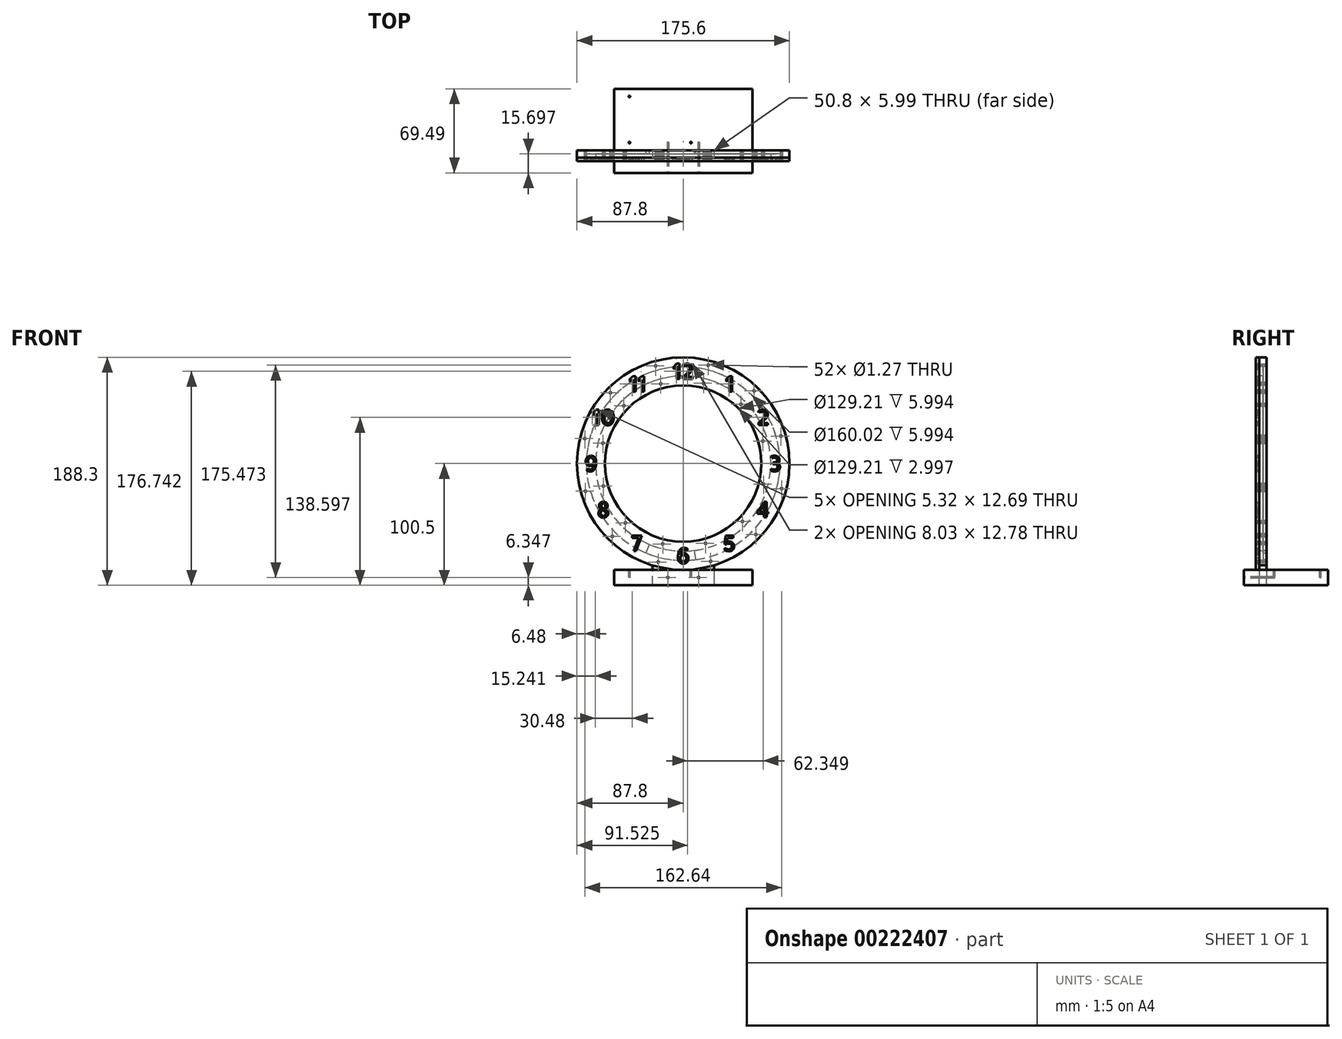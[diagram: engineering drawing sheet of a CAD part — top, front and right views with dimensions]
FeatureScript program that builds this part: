
annotation { "Feature Type Name" : "Feature", "Feature Type Description" : "" }
export const myFeature = defineFeature(function(context is Context, id is Id, definition is map)
    precondition{}
    {
        {
            var Q0;
            Q0=qCreatedBy(makeId("Front.planeOp"),FACE);
            var sketch = newSketch(context, id + "F0", { "sketchPlane" : qUnion([Q0])});
            skCircle(sketch, "E0", {"center": v(0, 0) * mm, "radius": 76.2 * mm, "construction": true});
            skCircle(sketch, "E1", {"center": v(0, 0) * mm, "radius": 64.6 * mm});
            skCircle(sketch, "E2", {"center": v(0, 0) * mm, "radius": 87.8 * mm});
            skPoint(sketch, "E3", {"position": v(76.2, 0) * mm});
            skPoint(sketch, "E4.1.0", {"position": v(66, 38.1) * mm});
            skPoint(sketch, "E4.2.0", {"position": v(38.1, 66) * mm});
            skPoint(sketch, "E5.0.3.0", {"position": v(0, 76.2) * mm});
            skPoint(sketch, "E5.0.4.0", {"position": v(-38.1, 66) * mm});
            skPoint(sketch, "E5.0.5.0", {"position": v(-66, 38.1) * mm});
            skPoint(sketch, "E5.0.6.0", {"position": v(-76.2, 0) * mm});
            skPoint(sketch, "E5.0.7.0", {"position": v(-66, -38.1) * mm});
            skPoint(sketch, "E5.0.8.0", {"position": v(-38.1, -66) * mm});
            skPoint(sketch, "E5.0.9.0", {"position": v(0, -76.2) * mm});
            skPoint(sketch, "E5.0.10.0", {"position": v(38.1, -66) * mm});
            skPoint(sketch, "E5.0.11.0", {"position": v(66, -38.1) * mm});
            skLineSegment(sketch, "E6", {"start": v(-64.6, 0) * mm, "end": v(-87.8, 0) * mm, "construction": true});
            skText(sketch, "E7", { "text": "8", "fontName": "AllertaStencil-Regular.ttf"});
            skText(sketch, "E8", { "text": "9", "fontName": "AllertaStencil-Regular.ttf"});
            skText(sketch, "E9", { "text": "10", "fontName": "AllertaStencil-Regular.ttf"});
            skText(sketch, "E10", { "text": "11", "fontName": "AllertaStencil-Regular.ttf"});
            skText(sketch, "E11", { "text": "12", "fontName": "AllertaStencil-Regular.ttf"});
            skText(sketch, "E12", { "text": "1", "fontName": "AllertaStencil-Regular.ttf"});
            skText(sketch, "E13", { "text": "2", "fontName": "AllertaStencil-Regular.ttf"});
            skText(sketch, "E14", { "text": "3", "fontName": "AllertaStencil-Regular.ttf"});
            skText(sketch, "E15", { "text": "4", "fontName": "AllertaStencil-Regular.ttf"});
            skText(sketch, "E16", { "text": "5", "fontName": "AllertaStencil-Regular.ttf"});
            skText(sketch, "E17", { "text": "6", "fontName": "AllertaStencil-Regular.ttf"});
            skText(sketch, "E18", { "text": "7", "fontName": "AllertaStencil-Regular.ttf"});
            const initialGuessF0  = {"E7": [-0.0712, -0.04445, 1, 0, 0.0127], "E8": [-0.08172, -0.00635, 1, 0, 0.0127], "E9": [-0.07572, 0.03175, 1, 0, 0.0127], "E10": [-0.04524, 0.05964, 1, 0, 0.0127], "E11": [-0.00892, 0.06985, 1, 0, 0.0127], "E12": [0.0346, 0.05964, 1, 0, 0.0127], "E13": [0.0607, 0.03175, 1, 0, 0.0127], "E14": [0.07123, -0.00635, 1, 0, 0.0127], "E15": [0.06061, -0.04445, 1, 0, 0.0127], "E16": [0.03296, -0.07234, 1, 0, 0.0127], "E17": [-0.00554, -0.08255, 1, 0, 0.0127], "E18": [-0.04322, -0.07234, 1, 0, 0.0127]};
            skSetInitialGuess(sketch, initialGuessF0);
            skSolve(sketch);
        }
        {
            var Q0;
            Q0=makeQuery(id+"F0.imprint","IMPRINT",FACE,{"disambiguationData":[TD([[makeQuery(id+"F0.imprint","IMPRINT",EDGE,{"derivedFrom":sQuery(id+"F0.wireOp",EDGE,"E1")}),-1.0]])]});
            var Q1;
            Q1=makeQuery(id+"F0.imprint","IMPRINT",FACE,{"disambiguationData":[TD([[makeQuery(id+"F0.imprint","IMPRINT",EDGE,{"derivedFrom":sQuery(id+"F0.wireOp",EDGE,"7d483e61-7cf5-47a1-b7c1-5da3358f1183.sketch_text.stroke-18")}),1.0]])]});
            var Q2;
            Q2=makeQuery(id+"F0.imprint","IMPRINT",FACE,{"disambiguationData":[TD([[makeQuery(id+"F0.imprint","IMPRINT",EDGE,{"derivedFrom":sQuery(id+"F0.wireOp",EDGE,"5f28f833-6790-40a1-bd5c-eccc9cb81e5d.sketch_text.stroke-18")}),1.0]])]});
            var Q3;
            Q3=makeQuery(id+"F0.imprint","IMPRINT",FACE,{"disambiguationData":[TD([[makeQuery(id+"F0.imprint","IMPRINT",EDGE,{"derivedFrom":sQuery(id+"F0.wireOp",EDGE,"a3df33ba-9ce7-4ff5-b274-9ab914acd171.sketch_text.stroke-11")}),1.0]])]});
            var Q4;
            Q4=makeQuery(id+"F0.imprint","IMPRINT",FACE,{"disambiguationData":[TD([[makeQuery(id+"F0.imprint","IMPRINT",EDGE,{"derivedFrom":sQuery(id+"F0.wireOp",EDGE,"7d1886ea-437e-4a37-8a7b-76c15135a165.sketch_text.stroke-17")}),1.0]])]});
            var Q5;
            Q5=makeQuery(id+"F0.imprint","IMPRINT",FACE,{"disambiguationData":[TD([[makeQuery(id+"F0.imprint","IMPRINT",EDGE,{"derivedFrom":sQuery(id+"F0.wireOp",EDGE,"7586e49b-87d7-49c5-a20d-2f4a87698a29.sketch_text.stroke-16")}),1.0]])]});
            var Q6;
            Q6=makeQuery(id+"F0.imprint","IMPRINT",FACE,{"disambiguationData":[TD([[makeQuery(id+"F0.imprint","IMPRINT",EDGE,{"derivedFrom":sQuery(id+"F0.wireOp",EDGE,"7586e49b-87d7-49c5-a20d-2f4a87698a29.sketch_text.stroke-23")}),1.0]])]});
            extrude(context, id + "F1", {"entities" : qUnion([Q0, Q1, Q2, Q3, Q4, Q5, Q6]), "depth" : 3 * mm});
        }
        {
            var Q0;
            Q0=makeQuery(id+"F1.opExtrude","CAP_FACE",FACE,{"disambiguationData":[OSD([sQuery(id+"F0.wireOp",EDGE,"E1"),sQuery(id+"F0.wireOp",EDGE,"E2"),sQuery(id+"F0.wireOp",EDGE,"de5beee3-762f-49d2-a0f4-ebe761830ab9.sketch_text.stroke-0"),sQuery(id+"F0.wireOp",EDGE,"de5beee3-762f-49d2-a0f4-ebe761830ab9.sketch_text.stroke-1"),sQuery(id+"F0.wireOp",EDGE,"de5beee3-762f-49d2-a0f4-ebe761830ab9.sketch_text.stroke-2"),sQuery(id+"F0.wireOp",EDGE,"de5beee3-762f-49d2-a0f4-ebe761830ab9.sketch_text.stroke-3"),sQuery(id+"F0.wireOp",EDGE,"de5beee3-762f-49d2-a0f4-ebe761830ab9.sketch_text.stroke-4"),sQuery(id+"F0.wireOp",EDGE,"de5beee3-762f-49d2-a0f4-ebe761830ab9.sketch_text.stroke-5"),sQuery(id+"F0.wireOp",EDGE,"de5beee3-762f-49d2-a0f4-ebe761830ab9.sketch_text.stroke-6"),sQuery(id+"F0.wireOp",EDGE,"de5beee3-762f-49d2-a0f4-ebe761830ab9.sketch_text.stroke-7"),sQuery(id+"F0.wireOp",EDGE,"de5beee3-762f-49d2-a0f4-ebe761830ab9.sketch_text.stroke-8"),sQuery(id+"F0.wireOp",EDGE,"de5beee3-762f-49d2-a0f4-ebe761830ab9.sketch_text.stroke-9"),sQuery(id+"F0.wireOp",EDGE,"de5beee3-762f-49d2-a0f4-ebe761830ab9.sketch_text.stroke-10"),sQuery(id+"F0.wireOp",EDGE,"de5beee3-762f-49d2-a0f4-ebe761830ab9.sketch_text.stroke-11"),sQuery(id+"F0.wireOp",EDGE,"de5beee3-762f-49d2-a0f4-ebe761830ab9.sketch_text.stroke-12"),sQuery(id+"F0.wireOp",EDGE,"de5beee3-762f-49d2-a0f4-ebe761830ab9.sketch_text.stroke-13"),sQuery(id+"F0.wireOp",EDGE,"de5beee3-762f-49d2-a0f4-ebe761830ab9.sketch_text.stroke-14"),sQuery(id+"F0.wireOp",EDGE,"de5beee3-762f-49d2-a0f4-ebe761830ab9.sketch_text.stroke-15"),sQuery(id+"F0.wireOp",EDGE,"de5beee3-762f-49d2-a0f4-ebe761830ab9.sketch_text.stroke-16"),sQuery(id+"F0.wireOp",EDGE,"de5beee3-762f-49d2-a0f4-ebe761830ab9.sketch_text.stroke-17"),sQuery(id+"F0.wireOp",EDGE,"de5beee3-762f-49d2-a0f4-ebe761830ab9.sketch_text.stroke-18"),sQuery(id+"F0.wireOp",EDGE,"de5beee3-762f-49d2-a0f4-ebe761830ab9.sketch_text.stroke-19"),sQuery(id+"F0.wireOp",EDGE,"de5beee3-762f-49d2-a0f4-ebe761830ab9.sketch_text.stroke-20"),sQuery(id+"F0.wireOp",EDGE,"de5beee3-762f-49d2-a0f4-ebe761830ab9.sketch_text.stroke-21"),sQuery(id+"F0.wireOp",EDGE,"de5beee3-762f-49d2-a0f4-ebe761830ab9.sketch_text.stroke-22"),sQuery(id+"F0.wireOp",EDGE,"de5beee3-762f-49d2-a0f4-ebe761830ab9.sketch_text.stroke-23"),sQuery(id+"F0.wireOp",EDGE,"de5beee3-762f-49d2-a0f4-ebe761830ab9.sketch_text.stroke-24"),sQuery(id+"F0.wireOp",EDGE,"de5beee3-762f-49d2-a0f4-ebe761830ab9.sketch_text.stroke-25"),sQuery(id+"F0.wireOp",EDGE,"de5beee3-762f-49d2-a0f4-ebe761830ab9.sketch_text.stroke-26"),sQuery(id+"F0.wireOp",EDGE,"de5beee3-762f-49d2-a0f4-ebe761830ab9.sketch_text.stroke-27"),sQuery(id+"F0.wireOp",EDGE,"de5beee3-762f-49d2-a0f4-ebe761830ab9.sketch_text.stroke-28"),sQuery(id+"F0.wireOp",EDGE,"de5beee3-762f-49d2-a0f4-ebe761830ab9.sketch_text.stroke-29"),sQuery(id+"F0.wireOp",EDGE,"de5beee3-762f-49d2-a0f4-ebe761830ab9.sketch_text.stroke-30"),sQuery(id+"F0.wireOp",EDGE,"de5beee3-762f-49d2-a0f4-ebe761830ab9.sketch_text.stroke-31"),sQuery(id+"F0.wireOp",EDGE,"de5beee3-762f-49d2-a0f4-ebe761830ab9.sketch_text.stroke-32"),sQuery(id+"F0.wireOp",EDGE,"de5beee3-762f-49d2-a0f4-ebe761830ab9.sketch_text.stroke-33"),sQuery(id+"F0.wireOp",EDGE,"b63be222-8b13-47c3-914a-0bf364170a45.sketch_text.stroke-0"),sQuery(id+"F0.wireOp",EDGE,"b63be222-8b13-47c3-914a-0bf364170a45.sketch_text.stroke-1"),sQuery(id+"F0.wireOp",EDGE,"b63be222-8b13-47c3-914a-0bf364170a45.sketch_text.stroke-2"),sQuery(id+"F0.wireOp",EDGE,"b63be222-8b13-47c3-914a-0bf364170a45.sketch_text.stroke-3"),sQuery(id+"F0.wireOp",EDGE,"b63be222-8b13-47c3-914a-0bf364170a45.sketch_text.stroke-4"),sQuery(id+"F0.wireOp",EDGE,"b63be222-8b13-47c3-914a-0bf364170a45.sketch_text.stroke-5"),sQuery(id+"F0.wireOp",EDGE,"b63be222-8b13-47c3-914a-0bf364170a45.sketch_text.stroke-6"),sQuery(id+"F0.wireOp",EDGE,"b63be222-8b13-47c3-914a-0bf364170a45.sketch_text.stroke-7"),sQuery(id+"F0.wireOp",EDGE,"b63be222-8b13-47c3-914a-0bf364170a45.sketch_text.stroke-8"),sQuery(id+"F0.wireOp",EDGE,"b63be222-8b13-47c3-914a-0bf364170a45.sketch_text.stroke-9"),sQuery(id+"F0.wireOp",EDGE,"80047d97-1fc0-4e6f-9ae0-e87ff81d1daa.sketch_text.stroke-0"),sQuery(id+"F0.wireOp",EDGE,"80047d97-1fc0-4e6f-9ae0-e87ff81d1daa.sketch_text.stroke-1"),sQuery(id+"F0.wireOp",EDGE,"80047d97-1fc0-4e6f-9ae0-e87ff81d1daa.sketch_text.stroke-2"),sQuery(id+"F0.wireOp",EDGE,"80047d97-1fc0-4e6f-9ae0-e87ff81d1daa.sketch_text.stroke-3"),sQuery(id+"F0.wireOp",EDGE,"80047d97-1fc0-4e6f-9ae0-e87ff81d1daa.sketch_text.stroke-4"),sQuery(id+"F0.wireOp",EDGE,"80047d97-1fc0-4e6f-9ae0-e87ff81d1daa.sketch_text.stroke-5"),sQuery(id+"F0.wireOp",EDGE,"80047d97-1fc0-4e6f-9ae0-e87ff81d1daa.sketch_text.stroke-6"),sQuery(id+"F0.wireOp",EDGE,"80047d97-1fc0-4e6f-9ae0-e87ff81d1daa.sketch_text.stroke-7"),sQuery(id+"F0.wireOp",EDGE,"80047d97-1fc0-4e6f-9ae0-e87ff81d1daa.sketch_text.stroke-8"),sQuery(id+"F0.wireOp",EDGE,"80047d97-1fc0-4e6f-9ae0-e87ff81d1daa.sketch_text.stroke-9"),sQuery(id+"F0.wireOp",EDGE,"80047d97-1fc0-4e6f-9ae0-e87ff81d1daa.sketch_text.stroke-10"),sQuery(id+"F0.wireOp",EDGE,"80047d97-1fc0-4e6f-9ae0-e87ff81d1daa.sketch_text.stroke-11"),sQuery(id+"F0.wireOp",EDGE,"80047d97-1fc0-4e6f-9ae0-e87ff81d1daa.sketch_text.stroke-12"),sQuery(id+"F0.wireOp",EDGE,"80047d97-1fc0-4e6f-9ae0-e87ff81d1daa.sketch_text.stroke-13"),sQuery(id+"F0.wireOp",EDGE,"80047d97-1fc0-4e6f-9ae0-e87ff81d1daa.sketch_text.stroke-14"),sQuery(id+"F0.wireOp",EDGE,"80047d97-1fc0-4e6f-9ae0-e87ff81d1daa.sketch_text.stroke-15"),sQuery(id+"F0.wireOp",EDGE,"80047d97-1fc0-4e6f-9ae0-e87ff81d1daa.sketch_text.stroke-16"),sQuery(id+"F0.wireOp",EDGE,"80047d97-1fc0-4e6f-9ae0-e87ff81d1daa.sketch_text.stroke-17"),sQuery(id+"F0.wireOp",EDGE,"80047d97-1fc0-4e6f-9ae0-e87ff81d1daa.sketch_text.stroke-18"),sQuery(id+"F0.wireOp",EDGE,"80047d97-1fc0-4e6f-9ae0-e87ff81d1daa.sketch_text.stroke-19"),sQuery(id+"F0.wireOp",EDGE,"80047d97-1fc0-4e6f-9ae0-e87ff81d1daa.sketch_text.stroke-20"),sQuery(id+"F0.wireOp",EDGE,"80047d97-1fc0-4e6f-9ae0-e87ff81d1daa.sketch_text.stroke-21"),sQuery(id+"F0.wireOp",EDGE,"80047d97-1fc0-4e6f-9ae0-e87ff81d1daa.sketch_text.stroke-22"),sQuery(id+"F0.wireOp",EDGE,"80047d97-1fc0-4e6f-9ae0-e87ff81d1daa.sketch_text.stroke-23"),sQuery(id+"F0.wireOp",EDGE,"b786957e-899e-43aa-b801-9e3ba5b127da.sketch_text.stroke-0"),sQuery(id+"F0.wireOp",EDGE,"b786957e-899e-43aa-b801-9e3ba5b127da.sketch_text.stroke-1"),sQuery(id+"F0.wireOp",EDGE,"b786957e-899e-43aa-b801-9e3ba5b127da.sketch_text.stroke-2"),sQuery(id+"F0.wireOp",EDGE,"b786957e-899e-43aa-b801-9e3ba5b127da.sketch_text.stroke-3"),sQuery(id+"F0.wireOp",EDGE,"b786957e-899e-43aa-b801-9e3ba5b127da.sketch_text.stroke-4"),sQuery(id+"F0.wireOp",EDGE,"b786957e-899e-43aa-b801-9e3ba5b127da.sketch_text.stroke-5"),sQuery(id+"F0.wireOp",EDGE,"b786957e-899e-43aa-b801-9e3ba5b127da.sketch_text.stroke-6"),sQuery(id+"F0.wireOp",EDGE,"b786957e-899e-43aa-b801-9e3ba5b127da.sketch_text.stroke-7"),sQuery(id+"F0.wireOp",EDGE,"b786957e-899e-43aa-b801-9e3ba5b127da.sketch_text.stroke-8"),sQuery(id+"F0.wireOp",EDGE,"b786957e-899e-43aa-b801-9e3ba5b127da.sketch_text.stroke-9"),sQuery(id+"F0.wireOp",EDGE,"b786957e-899e-43aa-b801-9e3ba5b127da.sketch_text.stroke-10"),sQuery(id+"F0.wireOp",EDGE,"b786957e-899e-43aa-b801-9e3ba5b127da.sketch_text.stroke-11"),sQuery(id+"F0.wireOp",EDGE,"b786957e-899e-43aa-b801-9e3ba5b127da.sketch_text.stroke-12"),sQuery(id+"F0.wireOp",EDGE,"b786957e-899e-43aa-b801-9e3ba5b127da.sketch_text.stroke-13"),sQuery(id+"F0.wireOp",EDGE,"b786957e-899e-43aa-b801-9e3ba5b127da.sketch_text.stroke-14"),sQuery(id+"F0.wireOp",EDGE,"b786957e-899e-43aa-b801-9e3ba5b127da.sketch_text.stroke-15"),sQuery(id+"F0.wireOp",EDGE,"b786957e-899e-43aa-b801-9e3ba5b127da.sketch_text.stroke-16"),sQuery(id+"F0.wireOp",EDGE,"b786957e-899e-43aa-b801-9e3ba5b127da.sketch_text.stroke-17"),sQuery(id+"F0.wireOp",EDGE,"b786957e-899e-43aa-b801-9e3ba5b127da.sketch_text.stroke-18"),sQuery(id+"F0.wireOp",EDGE,"b786957e-899e-43aa-b801-9e3ba5b127da.sketch_text.stroke-19"),sQuery(id+"F0.wireOp",EDGE,"b786957e-899e-43aa-b801-9e3ba5b127da.sketch_text.stroke-20"),sQuery(id+"F0.wireOp",EDGE,"b786957e-899e-43aa-b801-9e3ba5b127da.sketch_text.stroke-21"),sQuery(id+"F0.wireOp",EDGE,"b786957e-899e-43aa-b801-9e3ba5b127da.sketch_text.stroke-22"),sQuery(id+"F0.wireOp",EDGE,"b786957e-899e-43aa-b801-9e3ba5b127da.sketch_text.stroke-23"),sQuery(id+"F0.wireOp",EDGE,"b786957e-899e-43aa-b801-9e3ba5b127da.sketch_text.stroke-24"),sQuery(id+"F0.wireOp",EDGE,"b786957e-899e-43aa-b801-9e3ba5b127da.sketch_text.stroke-25"),sQuery(id+"F0.wireOp",EDGE,"b786957e-899e-43aa-b801-9e3ba5b127da.sketch_text.stroke-26"),sQuery(id+"F0.wireOp",EDGE,"a3df33ba-9ce7-4ff5-b274-9ab914acd171.sketch_text.stroke-0"),sQuery(id+"F0.wireOp",EDGE,"a3df33ba-9ce7-4ff5-b274-9ab914acd171.sketch_text.stroke-1"),sQuery(id+"F0.wireOp",EDGE,"a3df33ba-9ce7-4ff5-b274-9ab914acd171.sketch_text.stroke-2"),sQuery(id+"F0.wireOp",EDGE,"a3df33ba-9ce7-4ff5-b274-9ab914acd171.sketch_text.stroke-3"),sQuery(id+"F0.wireOp",EDGE,"a3df33ba-9ce7-4ff5-b274-9ab914acd171.sketch_text.stroke-4"),sQuery(id+"F0.wireOp",EDGE,"a3df33ba-9ce7-4ff5-b274-9ab914acd171.sketch_text.stroke-5"),sQuery(id+"F0.wireOp",EDGE,"a3df33ba-9ce7-4ff5-b274-9ab914acd171.sketch_text.stroke-6"),sQuery(id+"F0.wireOp",EDGE,"a3df33ba-9ce7-4ff5-b274-9ab914acd171.sketch_text.stroke-7"),sQuery(id+"F0.wireOp",EDGE,"a3df33ba-9ce7-4ff5-b274-9ab914acd171.sketch_text.stroke-8"),sQuery(id+"F0.wireOp",EDGE,"a3df33ba-9ce7-4ff5-b274-9ab914acd171.sketch_text.stroke-9"),sQuery(id+"F0.wireOp",EDGE,"a3df33ba-9ce7-4ff5-b274-9ab914acd171.sketch_text.stroke-10"),sQuery(id+"F0.wireOp",EDGE,"f39d2274-3346-4c4b-a620-f063c4256d13.sketch_text.stroke-0"),sQuery(id+"F0.wireOp",EDGE,"f39d2274-3346-4c4b-a620-f063c4256d13.sketch_text.stroke-1"),sQuery(id+"F0.wireOp",EDGE,"f39d2274-3346-4c4b-a620-f063c4256d13.sketch_text.stroke-2"),sQuery(id+"F0.wireOp",EDGE,"f39d2274-3346-4c4b-a620-f063c4256d13.sketch_text.stroke-3"),sQuery(id+"F0.wireOp",EDGE,"f39d2274-3346-4c4b-a620-f063c4256d13.sketch_text.stroke-4"),sQuery(id+"F0.wireOp",EDGE,"f39d2274-3346-4c4b-a620-f063c4256d13.sketch_text.stroke-5"),sQuery(id+"F0.wireOp",EDGE,"f39d2274-3346-4c4b-a620-f063c4256d13.sketch_text.stroke-6"),sQuery(id+"F0.wireOp",EDGE,"f39d2274-3346-4c4b-a620-f063c4256d13.sketch_text.stroke-7"),sQuery(id+"F0.wireOp",EDGE,"f39d2274-3346-4c4b-a620-f063c4256d13.sketch_text.stroke-8"),sQuery(id+"F0.wireOp",EDGE,"f39d2274-3346-4c4b-a620-f063c4256d13.sketch_text.stroke-9"),sQuery(id+"F0.wireOp",EDGE,"f39d2274-3346-4c4b-a620-f063c4256d13.sketch_text.stroke-10"),sQuery(id+"F0.wireOp",EDGE,"f39d2274-3346-4c4b-a620-f063c4256d13.sketch_text.stroke-11"),sQuery(id+"F0.wireOp",EDGE,"f39d2274-3346-4c4b-a620-f063c4256d13.sketch_text.stroke-12"),sQuery(id+"F0.wireOp",EDGE,"f39d2274-3346-4c4b-a620-f063c4256d13.sketch_text.stroke-13"),sQuery(id+"F0.wireOp",EDGE,"f39d2274-3346-4c4b-a620-f063c4256d13.sketch_text.stroke-14"),sQuery(id+"F0.wireOp",EDGE,"f39d2274-3346-4c4b-a620-f063c4256d13.sketch_text.stroke-15"),sQuery(id+"F0.wireOp",EDGE,"f39d2274-3346-4c4b-a620-f063c4256d13.sketch_text.stroke-16"),sQuery(id+"F0.wireOp",EDGE,"f39d2274-3346-4c4b-a620-f063c4256d13.sketch_text.stroke-17"),sQuery(id+"F0.wireOp",EDGE,"f39d2274-3346-4c4b-a620-f063c4256d13.sketch_text.stroke-18"),sQuery(id+"F0.wireOp",EDGE,"f39d2274-3346-4c4b-a620-f063c4256d13.sketch_text.stroke-19"),sQuery(id+"F0.wireOp",EDGE,"7d1886ea-437e-4a37-8a7b-76c15135a165.sketch_text.stroke-0"),sQuery(id+"F0.wireOp",EDGE,"7d1886ea-437e-4a37-8a7b-76c15135a165.sketch_text.stroke-1"),sQuery(id+"F0.wireOp",EDGE,"7d1886ea-437e-4a37-8a7b-76c15135a165.sketch_text.stroke-2"),sQuery(id+"F0.wireOp",EDGE,"7d1886ea-437e-4a37-8a7b-76c15135a165.sketch_text.stroke-3"),sQuery(id+"F0.wireOp",EDGE,"7d1886ea-437e-4a37-8a7b-76c15135a165.sketch_text.stroke-4"),sQuery(id+"F0.wireOp",EDGE,"7d1886ea-437e-4a37-8a7b-76c15135a165.sketch_text.stroke-5"),sQuery(id+"F0.wireOp",EDGE,"7d1886ea-437e-4a37-8a7b-76c15135a165.sketch_text.stroke-6"),sQuery(id+"F0.wireOp",EDGE,"7d1886ea-437e-4a37-8a7b-76c15135a165.sketch_text.stroke-7"),sQuery(id+"F0.wireOp",EDGE,"7d1886ea-437e-4a37-8a7b-76c15135a165.sketch_text.stroke-8"),sQuery(id+"F0.wireOp",EDGE,"7d1886ea-437e-4a37-8a7b-76c15135a165.sketch_text.stroke-9"),sQuery(id+"F0.wireOp",EDGE,"7d1886ea-437e-4a37-8a7b-76c15135a165.sketch_text.stroke-10"),sQuery(id+"F0.wireOp",EDGE,"7d1886ea-437e-4a37-8a7b-76c15135a165.sketch_text.stroke-11"),sQuery(id+"F0.wireOp",EDGE,"7d1886ea-437e-4a37-8a7b-76c15135a165.sketch_text.stroke-12"),sQuery(id+"F0.wireOp",EDGE,"7d1886ea-437e-4a37-8a7b-76c15135a165.sketch_text.stroke-13"),sQuery(id+"F0.wireOp",EDGE,"7d1886ea-437e-4a37-8a7b-76c15135a165.sketch_text.stroke-14"),sQuery(id+"F0.wireOp",EDGE,"7d1886ea-437e-4a37-8a7b-76c15135a165.sketch_text.stroke-15"),sQuery(id+"F0.wireOp",EDGE,"7d1886ea-437e-4a37-8a7b-76c15135a165.sketch_text.stroke-16"),sQuery(id+"F0.wireOp",EDGE,"3925cc31-eec3-4944-acb0-ac977a0c5539.sketch_text.stroke-0"),sQuery(id+"F0.wireOp",EDGE,"3925cc31-eec3-4944-acb0-ac977a0c5539.sketch_text.stroke-1"),sQuery(id+"F0.wireOp",EDGE,"3925cc31-eec3-4944-acb0-ac977a0c5539.sketch_text.stroke-2"),sQuery(id+"F0.wireOp",EDGE,"3925cc31-eec3-4944-acb0-ac977a0c5539.sketch_text.stroke-3"),sQuery(id+"F0.wireOp",EDGE,"3925cc31-eec3-4944-acb0-ac977a0c5539.sketch_text.stroke-4"),sQuery(id+"F0.wireOp",EDGE,"3925cc31-eec3-4944-acb0-ac977a0c5539.sketch_text.stroke-5"),sQuery(id+"F0.wireOp",EDGE,"3925cc31-eec3-4944-acb0-ac977a0c5539.sketch_text.stroke-6"),sQuery(id+"F0.wireOp",EDGE,"7586e49b-87d7-49c5-a20d-2f4a87698a29.sketch_text.stroke-0"),sQuery(id+"F0.wireOp",EDGE,"7586e49b-87d7-49c5-a20d-2f4a87698a29.sketch_text.stroke-1"),sQuery(id+"F0.wireOp",EDGE,"7586e49b-87d7-49c5-a20d-2f4a87698a29.sketch_text.stroke-2"),sQuery(id+"F0.wireOp",EDGE,"7586e49b-87d7-49c5-a20d-2f4a87698a29.sketch_text.stroke-3"),sQuery(id+"F0.wireOp",EDGE,"7586e49b-87d7-49c5-a20d-2f4a87698a29.sketch_text.stroke-4"),sQuery(id+"F0.wireOp",EDGE,"7586e49b-87d7-49c5-a20d-2f4a87698a29.sketch_text.stroke-5"),sQuery(id+"F0.wireOp",EDGE,"7586e49b-87d7-49c5-a20d-2f4a87698a29.sketch_text.stroke-6"),sQuery(id+"F0.wireOp",EDGE,"7586e49b-87d7-49c5-a20d-2f4a87698a29.sketch_text.stroke-7"),sQuery(id+"F0.wireOp",EDGE,"7586e49b-87d7-49c5-a20d-2f4a87698a29.sketch_text.stroke-8"),sQuery(id+"F0.wireOp",EDGE,"7586e49b-87d7-49c5-a20d-2f4a87698a29.sketch_text.stroke-9"),sQuery(id+"F0.wireOp",EDGE,"7586e49b-87d7-49c5-a20d-2f4a87698a29.sketch_text.stroke-10"),sQuery(id+"F0.wireOp",EDGE,"7586e49b-87d7-49c5-a20d-2f4a87698a29.sketch_text.stroke-11"),sQuery(id+"F0.wireOp",EDGE,"7586e49b-87d7-49c5-a20d-2f4a87698a29.sketch_text.stroke-12"),sQuery(id+"F0.wireOp",EDGE,"7586e49b-87d7-49c5-a20d-2f4a87698a29.sketch_text.stroke-13"),sQuery(id+"F0.wireOp",EDGE,"7586e49b-87d7-49c5-a20d-2f4a87698a29.sketch_text.stroke-14"),sQuery(id+"F0.wireOp",EDGE,"7586e49b-87d7-49c5-a20d-2f4a87698a29.sketch_text.stroke-15"),sQuery(id+"F0.wireOp",EDGE,"7d483e61-7cf5-47a1-b7c1-5da3358f1183.sketch_text.stroke-0"),sQuery(id+"F0.wireOp",EDGE,"7d483e61-7cf5-47a1-b7c1-5da3358f1183.sketch_text.stroke-1"),sQuery(id+"F0.wireOp",EDGE,"7d483e61-7cf5-47a1-b7c1-5da3358f1183.sketch_text.stroke-2"),sQuery(id+"F0.wireOp",EDGE,"7d483e61-7cf5-47a1-b7c1-5da3358f1183.sketch_text.stroke-3"),sQuery(id+"F0.wireOp",EDGE,"7d483e61-7cf5-47a1-b7c1-5da3358f1183.sketch_text.stroke-4"),sQuery(id+"F0.wireOp",EDGE,"7d483e61-7cf5-47a1-b7c1-5da3358f1183.sketch_text.stroke-5"),sQuery(id+"F0.wireOp",EDGE,"7d483e61-7cf5-47a1-b7c1-5da3358f1183.sketch_text.stroke-6"),sQuery(id+"F0.wireOp",EDGE,"7d483e61-7cf5-47a1-b7c1-5da3358f1183.sketch_text.stroke-7"),sQuery(id+"F0.wireOp",EDGE,"7d483e61-7cf5-47a1-b7c1-5da3358f1183.sketch_text.stroke-8"),sQuery(id+"F0.wireOp",EDGE,"7d483e61-7cf5-47a1-b7c1-5da3358f1183.sketch_text.stroke-9"),sQuery(id+"F0.wireOp",EDGE,"7d483e61-7cf5-47a1-b7c1-5da3358f1183.sketch_text.stroke-10"),sQuery(id+"F0.wireOp",EDGE,"7d483e61-7cf5-47a1-b7c1-5da3358f1183.sketch_text.stroke-11"),sQuery(id+"F0.wireOp",EDGE,"7d483e61-7cf5-47a1-b7c1-5da3358f1183.sketch_text.stroke-12"),sQuery(id+"F0.wireOp",EDGE,"7d483e61-7cf5-47a1-b7c1-5da3358f1183.sketch_text.stroke-13"),sQuery(id+"F0.wireOp",EDGE,"7d483e61-7cf5-47a1-b7c1-5da3358f1183.sketch_text.stroke-14"),sQuery(id+"F0.wireOp",EDGE,"7d483e61-7cf5-47a1-b7c1-5da3358f1183.sketch_text.stroke-15"),sQuery(id+"F0.wireOp",EDGE,"7d483e61-7cf5-47a1-b7c1-5da3358f1183.sketch_text.stroke-16"),sQuery(id+"F0.wireOp",EDGE,"7d483e61-7cf5-47a1-b7c1-5da3358f1183.sketch_text.stroke-17"),sQuery(id+"F0.wireOp",EDGE,"5f28f833-6790-40a1-bd5c-eccc9cb81e5d.sketch_text.stroke-0"),sQuery(id+"F0.wireOp",EDGE,"5f28f833-6790-40a1-bd5c-eccc9cb81e5d.sketch_text.stroke-1"),sQuery(id+"F0.wireOp",EDGE,"5f28f833-6790-40a1-bd5c-eccc9cb81e5d.sketch_text.stroke-2"),sQuery(id+"F0.wireOp",EDGE,"5f28f833-6790-40a1-bd5c-eccc9cb81e5d.sketch_text.stroke-3"),sQuery(id+"F0.wireOp",EDGE,"5f28f833-6790-40a1-bd5c-eccc9cb81e5d.sketch_text.stroke-4"),sQuery(id+"F0.wireOp",EDGE,"5f28f833-6790-40a1-bd5c-eccc9cb81e5d.sketch_text.stroke-5"),sQuery(id+"F0.wireOp",EDGE,"5f28f833-6790-40a1-bd5c-eccc9cb81e5d.sketch_text.stroke-6"),sQuery(id+"F0.wireOp",EDGE,"5f28f833-6790-40a1-bd5c-eccc9cb81e5d.sketch_text.stroke-7"),sQuery(id+"F0.wireOp",EDGE,"5f28f833-6790-40a1-bd5c-eccc9cb81e5d.sketch_text.stroke-8"),sQuery(id+"F0.wireOp",EDGE,"5f28f833-6790-40a1-bd5c-eccc9cb81e5d.sketch_text.stroke-9"),sQuery(id+"F0.wireOp",EDGE,"5f28f833-6790-40a1-bd5c-eccc9cb81e5d.sketch_text.stroke-10"),sQuery(id+"F0.wireOp",EDGE,"5f28f833-6790-40a1-bd5c-eccc9cb81e5d.sketch_text.stroke-11"),sQuery(id+"F0.wireOp",EDGE,"5f28f833-6790-40a1-bd5c-eccc9cb81e5d.sketch_text.stroke-12"),sQuery(id+"F0.wireOp",EDGE,"5f28f833-6790-40a1-bd5c-eccc9cb81e5d.sketch_text.stroke-13"),sQuery(id+"F0.wireOp",EDGE,"5f28f833-6790-40a1-bd5c-eccc9cb81e5d.sketch_text.stroke-14"),sQuery(id+"F0.wireOp",EDGE,"5f28f833-6790-40a1-bd5c-eccc9cb81e5d.sketch_text.stroke-15"),sQuery(id+"F0.wireOp",EDGE,"5f28f833-6790-40a1-bd5c-eccc9cb81e5d.sketch_text.stroke-16"),sQuery(id+"F0.wireOp",EDGE,"5f28f833-6790-40a1-bd5c-eccc9cb81e5d.sketch_text.stroke-17"),sQuery(id+"F0.wireOp",EDGE,"1433cbed-d636-4e2b-84d4-e52dd68185f6.sketch_text.stroke-0"),sQuery(id+"F0.wireOp",EDGE,"1433cbed-d636-4e2b-84d4-e52dd68185f6.sketch_text.stroke-1"),sQuery(id+"F0.wireOp",EDGE,"1433cbed-d636-4e2b-84d4-e52dd68185f6.sketch_text.stroke-2"),sQuery(id+"F0.wireOp",EDGE,"1433cbed-d636-4e2b-84d4-e52dd68185f6.sketch_text.stroke-3"),sQuery(id+"F0.wireOp",EDGE,"1433cbed-d636-4e2b-84d4-e52dd68185f6.sketch_text.stroke-4"),sQuery(id+"F0.wireOp",EDGE,"1433cbed-d636-4e2b-84d4-e52dd68185f6.sketch_text.stroke-5"),sQuery(id+"F0.wireOp",EDGE,"1433cbed-d636-4e2b-84d4-e52dd68185f6.sketch_text.stroke-6"),sQuery(id+"F0.wireOp",EDGE,"1433cbed-d636-4e2b-84d4-e52dd68185f6.sketch_text.stroke-7"),sQuery(id+"F0.wireOp",EDGE,"1433cbed-d636-4e2b-84d4-e52dd68185f6.sketch_text.stroke-8"),sQuery(id+"F0.wireOp",EDGE,"1433cbed-d636-4e2b-84d4-e52dd68185f6.sketch_text.stroke-9"),sQuery(id+"F0.wireOp",EDGE,"1433cbed-d636-4e2b-84d4-e52dd68185f6.sketch_text.stroke-10"),sQuery(id+"F0.wireOp",EDGE,"1433cbed-d636-4e2b-84d4-e52dd68185f6.sketch_text.stroke-11"),sQuery(id+"F0.wireOp",EDGE,"1433cbed-d636-4e2b-84d4-e52dd68185f6.sketch_text.stroke-12"),sQuery(id+"F0.wireOp",EDGE,"1433cbed-d636-4e2b-84d4-e52dd68185f6.sketch_text.stroke-13"),sQuery(id+"F0.wireOp",EDGE,"1433cbed-d636-4e2b-84d4-e52dd68185f6.sketch_text.stroke-14"),sQuery(id+"F0.wireOp",EDGE,"1433cbed-d636-4e2b-84d4-e52dd68185f6.sketch_text.stroke-15"),sQuery(id+"F0.wireOp",EDGE,"1433cbed-d636-4e2b-84d4-e52dd68185f6.sketch_text.stroke-16"),sQuery(id+"F0.wireOp",EDGE,"1433cbed-d636-4e2b-84d4-e52dd68185f6.sketch_text.stroke-17"),sQuery(id+"F0.wireOp",EDGE,"1433cbed-d636-4e2b-84d4-e52dd68185f6.sketch_text.stroke-18"),sQuery(id+"F0.wireOp",EDGE,"1433cbed-d636-4e2b-84d4-e52dd68185f6.sketch_text.stroke-19")])],"isStart":true});
            var sketch = newSketch(context, id + "F2", { "sketchPlane" : qUnion([Q0])});
            skCircle(sketch, "E19", {"center": v(0, 0) * mm, "radius": 76.2 * mm, "construction": true});
            skCircle(sketch, "E20.0", {"center": v(0, 0) * mm, "radius": 79.38 * mm});
            skCircle(sketch, "E21.0", {"center": v(0, 0) * mm, "radius": 73.03 * mm});
            skSolve(sketch);
        }
        {
            var Q0;
            Q0=makeQuery(id+"F2.imprint","IMPRINT",FACE,{"disambiguationData":[TD([[makeQuery(id+"F2.imprint","IMPRINT",EDGE,{"derivedFrom":makeQuery(id+"F1.opExtrude","CAP_EDGE",EDGE,{"disambiguationData":[OSD([sQuery(id+"F0.wireOp",EDGE,"E1")])],"isStart":true})}),-1.0]])]});
            var sketch = newSketch(context, id + "F3", { "sketchPlane" : qUnion([Q0])});
            skCircle(sketch, "E22.0", {"center": v(0, 0) * mm, "radius": 87.8 * mm});
            skCircle(sketch, "E23.0", {"center": v(0, 0) * mm, "radius": 64.6 * mm});
            skLineSegment(sketch, "E24", {"start": v(-25.4, -84.05) * mm, "end": v(-25.4, -100.5) * mm});
            skLineSegment(sketch, "E25", {"start": v(-25.4, -100.5) * mm, "end": v(25.4, -100.5) * mm});
            skLineSegment(sketch, "E26", {"start": v(25.4, -100.5) * mm, "end": v(25.4, -84.05) * mm});
            skLineSegment(sketch, "E27", {"start": v(0, -87.8) * mm, "end": v(0, -100.5) * mm});
            skSolve(sketch);
        }
        {
            var Q0;
            Q0 = qSketchRegion(id + "F3", true);
            extrude(context, id + "F4", {"entities" : qUnion([Q0]), "depth" : 6 * mm});
        }
        {
            var Q0;
            Q0=makeQuery(id+"F4.opExtrude","SWEPT_FACE",FACE,{"disambiguationData":[OSD([sQuery(id+"F3.wireOp",EDGE,"E25")])]});
            var sketch = newSketch(context, id + "F5", { "sketchPlane" : qUnion([Q0])});
            skLineSegment(sketch, "E28.bottom", {"start": v(-57.15, 12.7) * mm, "end": v(57.15, 12.7) * mm});
            skLineSegment(sketch, "E28.top", {"start": v(-57.15, -56.8) * mm, "end": v(57.15, -56.8) * mm});
            skLineSegment(sketch, "E28.left", {"start": v(-57.15, 12.7) * mm, "end": v(-57.15, -56.8) * mm});
            skLineSegment(sketch, "E28.right", {"start": v(57.15, 12.7) * mm, "end": v(57.15, -56.8) * mm});
            skLineSegment(sketch, "E29", {"start": v(0, 12.7) * mm, "end": v(0, -56.8) * mm, "construction": true});
            skLineSegment(sketch, "E30", {"start": v(-57.15, -22.05) * mm, "end": v(57.15, -22.05) * mm, "construction": true});
            skPoint(sketch, "E31", {"position": v(0, -22.05) * mm});
            skSolve(sketch);
        }
        {
            var Q0;
            Q0=makeQuery(id+"F5.imprint","IMPRINT",FACE,{"disambiguationData":[TD([[makeQuery(id+"F5.imprint","IMPRINT",EDGE,{"derivedFrom":sQuery(id+"F5.wireOp",EDGE,"E28.bottom")}),-1.0]])]});
            extrude(context, id + "F6", {"entities" : qUnion([Q0]), "oppositeDirection" : true, "depth" : 12.7 * mm});
        }
        {
            var Q0;
            Q0=makeQuery(id+"F2.imprint","IMPRINT",FACE,{"disambiguationData":[TD([[makeQuery(id+"F2.imprint","IMPRINT",EDGE,{"derivedFrom":makeQuery(id+"F1.opExtrude","CAP_EDGE",EDGE,{"disambiguationData":[OSD([sQuery(id+"F0.wireOp",EDGE,"E2")])],"isStart":true})}),-1.0]])]});
            var sketch = newSketch(context, id + "F7", { "sketchPlane" : qUnion([Q0])});
            skCircle(sketch, "E32", {"center": v(0, 0) * mm, "radius": 80 * mm});
            skCircle(sketch, "E33", {"center": v(0, 0) * mm, "radius": 72.4 * mm});
            skLineSegment(sketch, "E34", {"start": v(80, 0) * mm, "end": v(72.4, 0) * mm, "construction": true});
            skCircle(sketch, "E35", {"center": v(0, 0) * mm, "radius": 76.2 * mm, "construction": true});
            skPoint(sketch, "E36", {"position": v(76.2, 0) * mm});
            skSolve(sketch);
        }
        {
            var Q0;
            Q0 = qSketchRegion(id + "F7", true);
            extrude(context, id + "F8", {"entities" : qUnion([Q0]), "operationType" : NewBodyOperationType.REMOVE, "depth" : 3.17 * mm});
        }
        {
            var Q0;
            Q0=makeQuery(id+"F6.opExtrude","CAP_FACE",FACE,{"disambiguationData":[OSD([sQuery(id+"F3.wireOp",EDGE,"E24"),sQuery(id+"F3.wireOp",EDGE,"E25"),sQuery(id+"F3.wireOp",EDGE,"E26"),sQuery(id+"F5.wireOp",EDGE,"E28.bottom"),sQuery(id+"F5.wireOp",EDGE,"E28.top"),sQuery(id+"F5.wireOp",EDGE,"E28.left"),sQuery(id+"F5.wireOp",EDGE,"E28.right")])],"isStart":false});
            var sketch = newSketch(context, id + "F9", { "sketchPlane" : qUnion([Q0])});
            skLineSegment(sketch, "E37.bottom", {"start": v(-44.45, 50.44) * mm, "end": v(6.35, 50.44) * mm, "construction": true});
            skLineSegment(sketch, "E37.top", {"start": v(-44.45, 12.34) * mm, "end": v(6.35, 12.34) * mm, "construction": true});
            skLineSegment(sketch, "E37.left", {"start": v(-44.45, 50.44) * mm, "end": v(-44.45, 12.34) * mm, "construction": true});
            skLineSegment(sketch, "E37.right", {"start": v(6.35, 50.44) * mm, "end": v(6.35, 12.34) * mm, "construction": true});
            skCircle(sketch, "E38", {"center": v(-44.45, 50.44) * mm, "radius": 0.64 * mm});
            skCircle(sketch, "E39", {"center": v(-44.45, 12.34) * mm, "radius": 0.64 * mm});
            skCircle(sketch, "E40", {"center": v(6.35, 12.34) * mm, "radius": 0.64 * mm});
            skLineSegment(sketch, "E41", {"start": v(0, 6) * mm, "end": v(0, 56.8) * mm, "construction": true});
            skSolve(sketch);
        }
        {
            var Q0;
            Q0 = qSketchRegion(id + "F9", true);
            extrude(context, id + "F10", {"entities" : qUnion([Q0]), "operationType" : NewBodyOperationType.REMOVE, "oppositeDirection" : true, "depth" : 6.35 * mm});
        }
        {
            var Q0;
            Q0=makeQuery(id+"F1.opExtrude","CAP_FACE",FACE,{"disambiguationData":[OSD([sQuery(id+"F0.wireOp",EDGE,"E1"),sQuery(id+"F0.wireOp",EDGE,"E2"),sQuery(id+"F0.wireOp",EDGE,"E7.sketch_text.stroke-0"),sQuery(id+"F0.wireOp",EDGE,"E7.sketch_text.stroke-1"),sQuery(id+"F0.wireOp",EDGE,"E7.sketch_text.stroke-2"),sQuery(id+"F0.wireOp",EDGE,"E7.sketch_text.stroke-3"),sQuery(id+"F0.wireOp",EDGE,"E7.sketch_text.stroke-4"),sQuery(id+"F0.wireOp",EDGE,"E7.sketch_text.stroke-5"),sQuery(id+"F0.wireOp",EDGE,"E7.sketch_text.stroke-6"),sQuery(id+"F0.wireOp",EDGE,"E7.sketch_text.stroke-7"),sQuery(id+"F0.wireOp",EDGE,"E7.sketch_text.stroke-8"),sQuery(id+"F0.wireOp",EDGE,"E7.sketch_text.stroke-9"),sQuery(id+"F0.wireOp",EDGE,"E7.sketch_text.stroke-10"),sQuery(id+"F0.wireOp",EDGE,"E7.sketch_text.stroke-11"),sQuery(id+"F0.wireOp",EDGE,"E7.sketch_text.stroke-12"),sQuery(id+"F0.wireOp",EDGE,"E7.sketch_text.stroke-13"),sQuery(id+"F0.wireOp",EDGE,"E7.sketch_text.stroke-14"),sQuery(id+"F0.wireOp",EDGE,"E7.sketch_text.stroke-15"),sQuery(id+"F0.wireOp",EDGE,"E7.sketch_text.stroke-16"),sQuery(id+"F0.wireOp",EDGE,"E7.sketch_text.stroke-17"),sQuery(id+"F0.wireOp",EDGE,"E7.sketch_text.stroke-18"),sQuery(id+"F0.wireOp",EDGE,"E7.sketch_text.stroke-19"),sQuery(id+"F0.wireOp",EDGE,"E7.sketch_text.stroke-20"),sQuery(id+"F0.wireOp",EDGE,"E7.sketch_text.stroke-21"),sQuery(id+"F0.wireOp",EDGE,"E7.sketch_text.stroke-22"),sQuery(id+"F0.wireOp",EDGE,"E7.sketch_text.stroke-23"),sQuery(id+"F0.wireOp",EDGE,"E7.sketch_text.stroke-24"),sQuery(id+"F0.wireOp",EDGE,"E7.sketch_text.stroke-25"),sQuery(id+"F0.wireOp",EDGE,"E7.sketch_text.stroke-26"),sQuery(id+"F0.wireOp",EDGE,"E7.sketch_text.stroke-27"),sQuery(id+"F0.wireOp",EDGE,"E7.sketch_text.stroke-28"),sQuery(id+"F0.wireOp",EDGE,"E7.sketch_text.stroke-29"),sQuery(id+"F0.wireOp",EDGE,"E7.sketch_text.stroke-30"),sQuery(id+"F0.wireOp",EDGE,"E7.sketch_text.stroke-31"),sQuery(id+"F0.wireOp",EDGE,"E7.sketch_text.stroke-32"),sQuery(id+"F0.wireOp",EDGE,"E7.sketch_text.stroke-33"),sQuery(id+"F0.wireOp",EDGE,"E7.sketch_text.stroke-34"),sQuery(id+"F0.wireOp",EDGE,"E7.sketch_text.stroke-35"),sQuery(id+"F0.wireOp",EDGE,"E7.sketch_text.stroke-36"),sQuery(id+"F0.wireOp",EDGE,"E7.sketch_text.stroke-37"),sQuery(id+"F0.wireOp",EDGE,"E7.sketch_text.stroke-38"),sQuery(id+"F0.wireOp",EDGE,"E7.sketch_text.stroke-39"),sQuery(id+"F0.wireOp",EDGE,"E7.sketch_text.stroke-40"),sQuery(id+"F0.wireOp",EDGE,"E7.sketch_text.stroke-41"),sQuery(id+"F0.wireOp",EDGE,"E7.sketch_text.stroke-42"),sQuery(id+"F0.wireOp",EDGE,"E7.sketch_text.stroke-43"),sQuery(id+"F0.wireOp",EDGE,"E7.sketch_text.stroke-44"),sQuery(id+"F0.wireOp",EDGE,"E7.sketch_text.stroke-45"),sQuery(id+"F0.wireOp",EDGE,"E7.sketch_text.stroke-46"),sQuery(id+"F0.wireOp",EDGE,"E7.sketch_text.stroke-47"),sQuery(id+"F0.wireOp",EDGE,"E7.sketch_text.stroke-48"),sQuery(id+"F0.wireOp",EDGE,"E7.sketch_text.stroke-49"),sQuery(id+"F0.wireOp",EDGE,"E7.sketch_text.stroke-50"),sQuery(id+"F0.wireOp",EDGE,"E7.sketch_text.stroke-51"),sQuery(id+"F0.wireOp",EDGE,"E7.sketch_text.stroke-52"),sQuery(id+"F0.wireOp",EDGE,"E7.sketch_text.stroke-53"),sQuery(id+"F0.wireOp",EDGE,"E8.sketch_text.stroke-0"),sQuery(id+"F0.wireOp",EDGE,"E8.sketch_text.stroke-1"),sQuery(id+"F0.wireOp",EDGE,"E8.sketch_text.stroke-2"),sQuery(id+"F0.wireOp",EDGE,"E8.sketch_text.stroke-3"),sQuery(id+"F0.wireOp",EDGE,"E8.sketch_text.stroke-4"),sQuery(id+"F0.wireOp",EDGE,"E8.sketch_text.stroke-5"),sQuery(id+"F0.wireOp",EDGE,"E8.sketch_text.stroke-6"),sQuery(id+"F0.wireOp",EDGE,"E8.sketch_text.stroke-7"),sQuery(id+"F0.wireOp",EDGE,"E8.sketch_text.stroke-8"),sQuery(id+"F0.wireOp",EDGE,"E8.sketch_text.stroke-9"),sQuery(id+"F0.wireOp",EDGE,"E8.sketch_text.stroke-10"),sQuery(id+"F0.wireOp",EDGE,"E8.sketch_text.stroke-11"),sQuery(id+"F0.wireOp",EDGE,"E8.sketch_text.stroke-12"),sQuery(id+"F0.wireOp",EDGE,"E8.sketch_text.stroke-13"),sQuery(id+"F0.wireOp",EDGE,"E8.sketch_text.stroke-14"),sQuery(id+"F0.wireOp",EDGE,"E8.sketch_text.stroke-15"),sQuery(id+"F0.wireOp",EDGE,"E8.sketch_text.stroke-16"),sQuery(id+"F0.wireOp",EDGE,"E8.sketch_text.stroke-17"),sQuery(id+"F0.wireOp",EDGE,"E8.sketch_text.stroke-18"),sQuery(id+"F0.wireOp",EDGE,"E8.sketch_text.stroke-19"),sQuery(id+"F0.wireOp",EDGE,"E8.sketch_text.stroke-20"),sQuery(id+"F0.wireOp",EDGE,"E8.sketch_text.stroke-21"),sQuery(id+"F0.wireOp",EDGE,"E8.sketch_text.stroke-22"),sQuery(id+"F0.wireOp",EDGE,"E8.sketch_text.stroke-23"),sQuery(id+"F0.wireOp",EDGE,"E8.sketch_text.stroke-24"),sQuery(id+"F0.wireOp",EDGE,"E8.sketch_text.stroke-25"),sQuery(id+"F0.wireOp",EDGE,"E8.sketch_text.stroke-26"),sQuery(id+"F0.wireOp",EDGE,"E8.sketch_text.stroke-27"),sQuery(id+"F0.wireOp",EDGE,"E8.sketch_text.stroke-28"),sQuery(id+"F0.wireOp",EDGE,"E8.sketch_text.stroke-29"),sQuery(id+"F0.wireOp",EDGE,"E8.sketch_text.stroke-30"),sQuery(id+"F0.wireOp",EDGE,"E8.sketch_text.stroke-31"),sQuery(id+"F0.wireOp",EDGE,"E8.sketch_text.stroke-32"),sQuery(id+"F0.wireOp",EDGE,"E8.sketch_text.stroke-33"),sQuery(id+"F0.wireOp",EDGE,"E8.sketch_text.stroke-34"),sQuery(id+"F0.wireOp",EDGE,"E8.sketch_text.stroke-35"),sQuery(id+"F0.wireOp",EDGE,"E8.sketch_text.stroke-36"),sQuery(id+"F0.wireOp",EDGE,"E8.sketch_text.stroke-37"),sQuery(id+"F0.wireOp",EDGE,"E8.sketch_text.stroke-38"),sQuery(id+"F0.wireOp",EDGE,"E8.sketch_text.stroke-39"),sQuery(id+"F0.wireOp",EDGE,"E8.sketch_text.stroke-40"),sQuery(id+"F0.wireOp",EDGE,"E8.sketch_text.stroke-41"),sQuery(id+"F0.wireOp",EDGE,"E8.sketch_text.stroke-42"),sQuery(id+"F0.wireOp",EDGE,"E8.sketch_text.stroke-43"),sQuery(id+"F0.wireOp",EDGE,"E8.sketch_text.stroke-44"),sQuery(id+"F0.wireOp",EDGE,"E9.sketch_text.stroke-0"),sQuery(id+"F0.wireOp",EDGE,"E9.sketch_text.stroke-1"),sQuery(id+"F0.wireOp",EDGE,"E9.sketch_text.stroke-2"),sQuery(id+"F0.wireOp",EDGE,"E9.sketch_text.stroke-3"),sQuery(id+"F0.wireOp",EDGE,"E9.sketch_text.stroke-4"),sQuery(id+"F0.wireOp",EDGE,"E9.sketch_text.stroke-5"),sQuery(id+"F0.wireOp",EDGE,"E9.sketch_text.stroke-6"),sQuery(id+"F0.wireOp",EDGE,"E9.sketch_text.stroke-7"),sQuery(id+"F0.wireOp",EDGE,"E9.sketch_text.stroke-8"),sQuery(id+"F0.wireOp",EDGE,"E9.sketch_text.stroke-9"),sQuery(id+"F0.wireOp",EDGE,"E9.sketch_text.stroke-10"),sQuery(id+"F0.wireOp",EDGE,"E9.sketch_text.stroke-11"),sQuery(id+"F0.wireOp",EDGE,"E9.sketch_text.stroke-12"),sQuery(id+"F0.wireOp",EDGE,"E9.sketch_text.stroke-13"),sQuery(id+"F0.wireOp",EDGE,"E9.sketch_text.stroke-14"),sQuery(id+"F0.wireOp",EDGE,"E9.sketch_text.stroke-15"),sQuery(id+"F0.wireOp",EDGE,"E9.sketch_text.stroke-16"),sQuery(id+"F0.wireOp",EDGE,"E9.sketch_text.stroke-17"),sQuery(id+"F0.wireOp",EDGE,"E9.sketch_text.stroke-18"),sQuery(id+"F0.wireOp",EDGE,"E9.sketch_text.stroke-19"),sQuery(id+"F0.wireOp",EDGE,"E9.sketch_text.stroke-20"),sQuery(id+"F0.wireOp",EDGE,"E9.sketch_text.stroke-21"),sQuery(id+"F0.wireOp",EDGE,"E9.sketch_text.stroke-22"),sQuery(id+"F0.wireOp",EDGE,"E9.sketch_text.stroke-23"),sQuery(id+"F0.wireOp",EDGE,"E9.sketch_text.stroke-24"),sQuery(id+"F0.wireOp",EDGE,"E9.sketch_text.stroke-25"),sQuery(id+"F0.wireOp",EDGE,"E9.sketch_text.stroke-26"),sQuery(id+"F0.wireOp",EDGE,"E9.sketch_text.stroke-27"),sQuery(id+"F0.wireOp",EDGE,"E9.sketch_text.stroke-28"),sQuery(id+"F0.wireOp",EDGE,"E9.sketch_text.stroke-29"),sQuery(id+"F0.wireOp",EDGE,"E9.sketch_text.stroke-30"),sQuery(id+"F0.wireOp",EDGE,"E9.sketch_text.stroke-31"),sQuery(id+"F0.wireOp",EDGE,"E9.sketch_text.stroke-32"),sQuery(id+"F0.wireOp",EDGE,"E9.sketch_text.stroke-33"),sQuery(id+"F0.wireOp",EDGE,"E9.sketch_text.stroke-34"),sQuery(id+"F0.wireOp",EDGE,"E9.sketch_text.stroke-35"),sQuery(id+"F0.wireOp",EDGE,"E9.sketch_text.stroke-36"),sQuery(id+"F0.wireOp",EDGE,"E9.sketch_text.stroke-37"),sQuery(id+"F0.wireOp",EDGE,"E9.sketch_text.stroke-38"),sQuery(id+"F0.wireOp",EDGE,"E9.sketch_text.stroke-39"),sQuery(id+"F0.wireOp",EDGE,"E10.sketch_text.stroke-0"),sQuery(id+"F0.wireOp",EDGE,"E10.sketch_text.stroke-1"),sQuery(id+"F0.wireOp",EDGE,"E10.sketch_text.stroke-2"),sQuery(id+"F0.wireOp",EDGE,"E10.sketch_text.stroke-3"),sQuery(id+"F0.wireOp",EDGE,"E10.sketch_text.stroke-4"),sQuery(id+"F0.wireOp",EDGE,"E10.sketch_text.stroke-5"),sQuery(id+"F0.wireOp",EDGE,"E10.sketch_text.stroke-6"),sQuery(id+"F0.wireOp",EDGE,"E10.sketch_text.stroke-7"),sQuery(id+"F0.wireOp",EDGE,"E10.sketch_text.stroke-8"),sQuery(id+"F0.wireOp",EDGE,"E10.sketch_text.stroke-9"),sQuery(id+"F0.wireOp",EDGE,"E10.sketch_text.stroke-10"),sQuery(id+"F0.wireOp",EDGE,"E10.sketch_text.stroke-11"),sQuery(id+"F0.wireOp",EDGE,"E10.sketch_text.stroke-12"),sQuery(id+"F0.wireOp",EDGE,"E10.sketch_text.stroke-13"),sQuery(id+"F0.wireOp",EDGE,"E11.sketch_text.stroke-0"),sQuery(id+"F0.wireOp",EDGE,"E11.sketch_text.stroke-1"),sQuery(id+"F0.wireOp",EDGE,"E11.sketch_text.stroke-2"),sQuery(id+"F0.wireOp",EDGE,"E11.sketch_text.stroke-3"),sQuery(id+"F0.wireOp",EDGE,"E11.sketch_text.stroke-4"),sQuery(id+"F0.wireOp",EDGE,"E11.sketch_text.stroke-5"),sQuery(id+"F0.wireOp",EDGE,"E11.sketch_text.stroke-6"),sQuery(id+"F0.wireOp",EDGE,"E11.sketch_text.stroke-7"),sQuery(id+"F0.wireOp",EDGE,"E11.sketch_text.stroke-8"),sQuery(id+"F0.wireOp",EDGE,"E11.sketch_text.stroke-9"),sQuery(id+"F0.wireOp",EDGE,"E11.sketch_text.stroke-10"),sQuery(id+"F0.wireOp",EDGE,"E11.sketch_text.stroke-11"),sQuery(id+"F0.wireOp",EDGE,"E11.sketch_text.stroke-12"),sQuery(id+"F0.wireOp",EDGE,"E11.sketch_text.stroke-13"),sQuery(id+"F0.wireOp",EDGE,"E11.sketch_text.stroke-14"),sQuery(id+"F0.wireOp",EDGE,"E11.sketch_text.stroke-15"),sQuery(id+"F0.wireOp",EDGE,"E11.sketch_text.stroke-16"),sQuery(id+"F0.wireOp",EDGE,"E11.sketch_text.stroke-17"),sQuery(id+"F0.wireOp",EDGE,"E11.sketch_text.stroke-18"),sQuery(id+"F0.wireOp",EDGE,"E11.sketch_text.stroke-19"),sQuery(id+"F0.wireOp",EDGE,"E11.sketch_text.stroke-20"),sQuery(id+"F0.wireOp",EDGE,"E11.sketch_text.stroke-21"),sQuery(id+"F0.wireOp",EDGE,"E11.sketch_text.stroke-22"),sQuery(id+"F0.wireOp",EDGE,"E11.sketch_text.stroke-23"),sQuery(id+"F0.wireOp",EDGE,"E11.sketch_text.stroke-24"),sQuery(id+"F0.wireOp",EDGE,"E11.sketch_text.stroke-25"),sQuery(id+"F0.wireOp",EDGE,"E11.sketch_text.stroke-26"),sQuery(id+"F0.wireOp",EDGE,"E11.sketch_text.stroke-27"),sQuery(id+"F0.wireOp",EDGE,"E11.sketch_text.stroke-28"),sQuery(id+"F0.wireOp",EDGE,"E11.sketch_text.stroke-29"),sQuery(id+"F0.wireOp",EDGE,"E11.sketch_text.stroke-30"),sQuery(id+"F0.wireOp",EDGE,"E11.sketch_text.stroke-31"),sQuery(id+"F0.wireOp",EDGE,"E11.sketch_text.stroke-32"),sQuery(id+"F0.wireOp",EDGE,"E11.sketch_text.stroke-33"),sQuery(id+"F0.wireOp",EDGE,"E11.sketch_text.stroke-34"),sQuery(id+"F0.wireOp",EDGE,"E11.sketch_text.stroke-35"),sQuery(id+"F0.wireOp",EDGE,"E11.sketch_text.stroke-36"),sQuery(id+"F0.wireOp",EDGE,"E11.sketch_text.stroke-37"),sQuery(id+"F0.wireOp",EDGE,"E11.sketch_text.stroke-38"),sQuery(id+"F0.wireOp",EDGE,"E11.sketch_text.stroke-39"),sQuery(id+"F0.wireOp",EDGE,"E12.sketch_text.stroke-0"),sQuery(id+"F0.wireOp",EDGE,"E12.sketch_text.stroke-1"),sQuery(id+"F0.wireOp",EDGE,"E12.sketch_text.stroke-2"),sQuery(id+"F0.wireOp",EDGE,"E12.sketch_text.stroke-3"),sQuery(id+"F0.wireOp",EDGE,"E12.sketch_text.stroke-4"),sQuery(id+"F0.wireOp",EDGE,"E12.sketch_text.stroke-5"),sQuery(id+"F0.wireOp",EDGE,"E12.sketch_text.stroke-6"),sQuery(id+"F0.wireOp",EDGE,"E13.sketch_text.stroke-0"),sQuery(id+"F0.wireOp",EDGE,"E13.sketch_text.stroke-1"),sQuery(id+"F0.wireOp",EDGE,"E13.sketch_text.stroke-2"),sQuery(id+"F0.wireOp",EDGE,"E13.sketch_text.stroke-3"),sQuery(id+"F0.wireOp",EDGE,"E13.sketch_text.stroke-4"),sQuery(id+"F0.wireOp",EDGE,"E13.sketch_text.stroke-5"),sQuery(id+"F0.wireOp",EDGE,"E13.sketch_text.stroke-6"),sQuery(id+"F0.wireOp",EDGE,"E13.sketch_text.stroke-7"),sQuery(id+"F0.wireOp",EDGE,"E13.sketch_text.stroke-8"),sQuery(id+"F0.wireOp",EDGE,"E13.sketch_text.stroke-9"),sQuery(id+"F0.wireOp",EDGE,"E13.sketch_text.stroke-10"),sQuery(id+"F0.wireOp",EDGE,"E13.sketch_text.stroke-11"),sQuery(id+"F0.wireOp",EDGE,"E13.sketch_text.stroke-12"),sQuery(id+"F0.wireOp",EDGE,"E13.sketch_text.stroke-13"),sQuery(id+"F0.wireOp",EDGE,"E13.sketch_text.stroke-14"),sQuery(id+"F0.wireOp",EDGE,"E13.sketch_text.stroke-15"),sQuery(id+"F0.wireOp",EDGE,"E13.sketch_text.stroke-16"),sQuery(id+"F0.wireOp",EDGE,"E13.sketch_text.stroke-17"),sQuery(id+"F0.wireOp",EDGE,"E13.sketch_text.stroke-18"),sQuery(id+"F0.wireOp",EDGE,"E13.sketch_text.stroke-19"),sQuery(id+"F0.wireOp",EDGE,"E13.sketch_text.stroke-20"),sQuery(id+"F0.wireOp",EDGE,"E13.sketch_text.stroke-21"),sQuery(id+"F0.wireOp",EDGE,"E13.sketch_text.stroke-22"),sQuery(id+"F0.wireOp",EDGE,"E13.sketch_text.stroke-23"),sQuery(id+"F0.wireOp",EDGE,"E13.sketch_text.stroke-24"),sQuery(id+"F0.wireOp",EDGE,"E13.sketch_text.stroke-25"),sQuery(id+"F0.wireOp",EDGE,"E13.sketch_text.stroke-26"),sQuery(id+"F0.wireOp",EDGE,"E13.sketch_text.stroke-27"),sQuery(id+"F0.wireOp",EDGE,"E13.sketch_text.stroke-28"),sQuery(id+"F0.wireOp",EDGE,"E13.sketch_text.stroke-29"),sQuery(id+"F0.wireOp",EDGE,"E13.sketch_text.stroke-30"),sQuery(id+"F0.wireOp",EDGE,"E13.sketch_text.stroke-31"),sQuery(id+"F0.wireOp",EDGE,"E13.sketch_text.stroke-32"),sQuery(id+"F0.wireOp",EDGE,"E14.sketch_text.stroke-0"),sQuery(id+"F0.wireOp",EDGE,"E14.sketch_text.stroke-1"),sQuery(id+"F0.wireOp",EDGE,"E14.sketch_text.stroke-2"),sQuery(id+"F0.wireOp",EDGE,"E14.sketch_text.stroke-3"),sQuery(id+"F0.wireOp",EDGE,"E14.sketch_text.stroke-4"),sQuery(id+"F0.wireOp",EDGE,"E14.sketch_text.stroke-5"),sQuery(id+"F0.wireOp",EDGE,"E14.sketch_text.stroke-6"),sQuery(id+"F0.wireOp",EDGE,"E14.sketch_text.stroke-7"),sQuery(id+"F0.wireOp",EDGE,"E14.sketch_text.stroke-8"),sQuery(id+"F0.wireOp",EDGE,"E14.sketch_text.stroke-9"),sQuery(id+"F0.wireOp",EDGE,"E14.sketch_text.stroke-10"),sQuery(id+"F0.wireOp",EDGE,"E14.sketch_text.stroke-11"),sQuery(id+"F0.wireOp",EDGE,"E14.sketch_text.stroke-12"),sQuery(id+"F0.wireOp",EDGE,"E14.sketch_text.stroke-13"),sQuery(id+"F0.wireOp",EDGE,"E14.sketch_text.stroke-14"),sQuery(id+"F0.wireOp",EDGE,"E14.sketch_text.stroke-15"),sQuery(id+"F0.wireOp",EDGE,"E14.sketch_text.stroke-16"),sQuery(id+"F0.wireOp",EDGE,"E14.sketch_text.stroke-17"),sQuery(id+"F0.wireOp",EDGE,"E14.sketch_text.stroke-18"),sQuery(id+"F0.wireOp",EDGE,"E14.sketch_text.stroke-19"),sQuery(id+"F0.wireOp",EDGE,"E14.sketch_text.stroke-20"),sQuery(id+"F0.wireOp",EDGE,"E14.sketch_text.stroke-21"),sQuery(id+"F0.wireOp",EDGE,"E14.sketch_text.stroke-23"),sQuery(id+"F0.wireOp",EDGE,"E14.sketch_text.stroke-24"),sQuery(id+"F0.wireOp",EDGE,"E14.sketch_text.stroke-25"),sQuery(id+"F0.wireOp",EDGE,"E14.sketch_text.stroke-26"),sQuery(id+"F0.wireOp",EDGE,"E14.sketch_text.stroke-27"),sQuery(id+"F0.wireOp",EDGE,"E14.sketch_text.stroke-28"),sQuery(id+"F0.wireOp",EDGE,"E14.sketch_text.stroke-29"),sQuery(id+"F0.wireOp",EDGE,"E14.sketch_text.stroke-30"),sQuery(id+"F0.wireOp",EDGE,"E14.sketch_text.stroke-31"),sQuery(id+"F0.wireOp",EDGE,"E14.sketch_text.stroke-32"),sQuery(id+"F0.wireOp",EDGE,"E14.sketch_text.stroke-33"),sQuery(id+"F0.wireOp",EDGE,"E14.sketch_text.stroke-34"),sQuery(id+"F0.wireOp",EDGE,"E14.sketch_text.stroke-35"),sQuery(id+"F0.wireOp",EDGE,"E14.sketch_text.stroke-36"),sQuery(id+"F0.wireOp",EDGE,"E14.sketch_text.stroke-37"),sQuery(id+"F0.wireOp",EDGE,"E14.sketch_text.stroke-38"),sQuery(id+"F0.wireOp",EDGE,"E14.sketch_text.stroke-39"),sQuery(id+"F0.wireOp",EDGE,"E14.sketch_text.stroke-40"),sQuery(id+"F0.wireOp",EDGE,"E14.sketch_text.stroke-41"),sQuery(id+"F0.wireOp",EDGE,"E14.sketch_text.stroke-42"),sQuery(id+"F0.wireOp",EDGE,"E14.sketch_text.stroke-43"),sQuery(id+"F0.wireOp",EDGE,"E14.sketch_text.stroke-44"),sQuery(id+"F0.wireOp",EDGE,"E14.sketch_text.stroke-45"),sQuery(id+"F0.wireOp",EDGE,"E15.sketch_text.stroke-0"),sQuery(id+"F0.wireOp",EDGE,"E15.sketch_text.stroke-1"),sQuery(id+"F0.wireOp",EDGE,"E15.sketch_text.stroke-2"),sQuery(id+"F0.wireOp",EDGE,"E15.sketch_text.stroke-3"),sQuery(id+"F0.wireOp",EDGE,"E15.sketch_text.stroke-4"),sQuery(id+"F0.wireOp",EDGE,"E15.sketch_text.stroke-5"),sQuery(id+"F0.wireOp",EDGE,"E15.sketch_text.stroke-6"),sQuery(id+"F0.wireOp",EDGE,"E15.sketch_text.stroke-7"),sQuery(id+"F0.wireOp",EDGE,"E15.sketch_text.stroke-8"),sQuery(id+"F0.wireOp",EDGE,"E15.sketch_text.stroke-9"),sQuery(id+"F0.wireOp",EDGE,"E15.sketch_text.stroke-10"),sQuery(id+"F0.wireOp",EDGE,"E15.sketch_text.stroke-11"),sQuery(id+"F0.wireOp",EDGE,"E15.sketch_text.stroke-12"),sQuery(id+"F0.wireOp",EDGE,"E15.sketch_text.stroke-13"),sQuery(id+"F0.wireOp",EDGE,"E15.sketch_text.stroke-14"),sQuery(id+"F0.wireOp",EDGE,"E16.sketch_text.stroke-0"),sQuery(id+"F0.wireOp",EDGE,"E16.sketch_text.stroke-1"),sQuery(id+"F0.wireOp",EDGE,"E16.sketch_text.stroke-2"),sQuery(id+"F0.wireOp",EDGE,"E16.sketch_text.stroke-3"),sQuery(id+"F0.wireOp",EDGE,"E16.sketch_text.stroke-4"),sQuery(id+"F0.wireOp",EDGE,"E16.sketch_text.stroke-5"),sQuery(id+"F0.wireOp",EDGE,"E16.sketch_text.stroke-6"),sQuery(id+"F0.wireOp",EDGE,"E16.sketch_text.stroke-7"),sQuery(id+"F0.wireOp",EDGE,"E16.sketch_text.stroke-8"),sQuery(id+"F0.wireOp",EDGE,"E16.sketch_text.stroke-9"),sQuery(id+"F0.wireOp",EDGE,"E16.sketch_text.stroke-10"),sQuery(id+"F0.wireOp",EDGE,"E16.sketch_text.stroke-11"),sQuery(id+"F0.wireOp",EDGE,"E16.sketch_text.stroke-12"),sQuery(id+"F0.wireOp",EDGE,"E16.sketch_text.stroke-13"),sQuery(id+"F0.wireOp",EDGE,"E16.sketch_text.stroke-14"),sQuery(id+"F0.wireOp",EDGE,"E16.sketch_text.stroke-15"),sQuery(id+"F0.wireOp",EDGE,"E16.sketch_text.stroke-16"),sQuery(id+"F0.wireOp",EDGE,"E16.sketch_text.stroke-17"),sQuery(id+"F0.wireOp",EDGE,"E16.sketch_text.stroke-18"),sQuery(id+"F0.wireOp",EDGE,"E16.sketch_text.stroke-19"),sQuery(id+"F0.wireOp",EDGE,"E16.sketch_text.stroke-20"),sQuery(id+"F0.wireOp",EDGE,"E16.sketch_text.stroke-21"),sQuery(id+"F0.wireOp",EDGE,"E16.sketch_text.stroke-22"),sQuery(id+"F0.wireOp",EDGE,"E16.sketch_text.stroke-23"),sQuery(id+"F0.wireOp",EDGE,"E16.sketch_text.stroke-24"),sQuery(id+"F0.wireOp",EDGE,"E16.sketch_text.stroke-25"),sQuery(id+"F0.wireOp",EDGE,"E16.sketch_text.stroke-26"),sQuery(id+"F0.wireOp",EDGE,"E16.sketch_text.stroke-27"),sQuery(id+"F0.wireOp",EDGE,"E16.sketch_text.stroke-28"),sQuery(id+"F0.wireOp",EDGE,"E16.sketch_text.stroke-29"),sQuery(id+"F0.wireOp",EDGE,"E16.sketch_text.stroke-30"),sQuery(id+"F0.wireOp",EDGE,"E16.sketch_text.stroke-31"),sQuery(id+"F0.wireOp",EDGE,"E16.sketch_text.stroke-32"),sQuery(id+"F0.wireOp",EDGE,"E16.sketch_text.stroke-33"),sQuery(id+"F0.wireOp",EDGE,"E16.sketch_text.stroke-34"),sQuery(id+"F0.wireOp",EDGE,"E16.sketch_text.stroke-35"),sQuery(id+"F0.wireOp",EDGE,"E16.sketch_text.stroke-36"),sQuery(id+"F0.wireOp",EDGE,"E16.sketch_text.stroke-37"),sQuery(id+"F0.wireOp",EDGE,"E16.sketch_text.stroke-38"),sQuery(id+"F0.wireOp",EDGE,"E16.sketch_text.stroke-39"),sQuery(id+"F0.wireOp",EDGE,"E16.sketch_text.stroke-40"),sQuery(id+"F0.wireOp",EDGE,"E17.sketch_text.stroke-0"),sQuery(id+"F0.wireOp",EDGE,"E17.sketch_text.stroke-1"),sQuery(id+"F0.wireOp",EDGE,"E17.sketch_text.stroke-2"),sQuery(id+"F0.wireOp",EDGE,"E17.sketch_text.stroke-3"),sQuery(id+"F0.wireOp",EDGE,"E17.sketch_text.stroke-4"),sQuery(id+"F0.wireOp",EDGE,"E17.sketch_text.stroke-5"),sQuery(id+"F0.wireOp",EDGE,"E17.sketch_text.stroke-6"),sQuery(id+"F0.wireOp",EDGE,"E17.sketch_text.stroke-7"),sQuery(id+"F0.wireOp",EDGE,"E17.sketch_text.stroke-8"),sQuery(id+"F0.wireOp",EDGE,"E17.sketch_text.stroke-9"),sQuery(id+"F0.wireOp",EDGE,"E17.sketch_text.stroke-10"),sQuery(id+"F0.wireOp",EDGE,"E17.sketch_text.stroke-11"),sQuery(id+"F0.wireOp",EDGE,"E17.sketch_text.stroke-12"),sQuery(id+"F0.wireOp",EDGE,"E17.sketch_text.stroke-13"),sQuery(id+"F0.wireOp",EDGE,"E17.sketch_text.stroke-14"),sQuery(id+"F0.wireOp",EDGE,"E17.sketch_text.stroke-15"),sQuery(id+"F0.wireOp",EDGE,"E17.sketch_text.stroke-16"),sQuery(id+"F0.wireOp",EDGE,"E17.sketch_text.stroke-17"),sQuery(id+"F0.wireOp",EDGE,"E17.sketch_text.stroke-18"),sQuery(id+"F0.wireOp",EDGE,"E17.sketch_text.stroke-19"),sQuery(id+"F0.wireOp",EDGE,"E17.sketch_text.stroke-20"),sQuery(id+"F0.wireOp",EDGE,"E17.sketch_text.stroke-21"),sQuery(id+"F0.wireOp",EDGE,"E17.sketch_text.stroke-22"),sQuery(id+"F0.wireOp",EDGE,"E17.sketch_text.stroke-23"),sQuery(id+"F0.wireOp",EDGE,"E17.sketch_text.stroke-24"),sQuery(id+"F0.wireOp",EDGE,"E17.sketch_text.stroke-25"),sQuery(id+"F0.wireOp",EDGE,"E17.sketch_text.stroke-26"),sQuery(id+"F0.wireOp",EDGE,"E17.sketch_text.stroke-27"),sQuery(id+"F0.wireOp",EDGE,"E17.sketch_text.stroke-28"),sQuery(id+"F0.wireOp",EDGE,"E17.sketch_text.stroke-29"),sQuery(id+"F0.wireOp",EDGE,"E17.sketch_text.stroke-30"),sQuery(id+"F0.wireOp",EDGE,"E17.sketch_text.stroke-31"),sQuery(id+"F0.wireOp",EDGE,"E17.sketch_text.stroke-32"),sQuery(id+"F0.wireOp",EDGE,"E17.sketch_text.stroke-33"),sQuery(id+"F0.wireOp",EDGE,"E17.sketch_text.stroke-34"),sQuery(id+"F0.wireOp",EDGE,"E17.sketch_text.stroke-35"),sQuery(id+"F0.wireOp",EDGE,"E17.sketch_text.stroke-36"),sQuery(id+"F0.wireOp",EDGE,"E17.sketch_text.stroke-37"),sQuery(id+"F0.wireOp",EDGE,"E17.sketch_text.stroke-38"),sQuery(id+"F0.wireOp",EDGE,"E17.sketch_text.stroke-39"),sQuery(id+"F0.wireOp",EDGE,"E17.sketch_text.stroke-40"),sQuery(id+"F0.wireOp",EDGE,"E17.sketch_text.stroke-41"),sQuery(id+"F0.wireOp",EDGE,"E17.sketch_text.stroke-42"),sQuery(id+"F0.wireOp",EDGE,"E17.sketch_text.stroke-43"),sQuery(id+"F0.wireOp",EDGE,"E17.sketch_text.stroke-44"),sQuery(id+"F0.wireOp",EDGE,"E18.sketch_text.stroke-0"),sQuery(id+"F0.wireOp",EDGE,"E18.sketch_text.stroke-1"),sQuery(id+"F0.wireOp",EDGE,"E18.sketch_text.stroke-2"),sQuery(id+"F0.wireOp",EDGE,"E18.sketch_text.stroke-3"),sQuery(id+"F0.wireOp",EDGE,"E18.sketch_text.stroke-4"),sQuery(id+"F0.wireOp",EDGE,"E18.sketch_text.stroke-5")])],"isStart":false});
            var sketch = newSketch(context, id + "F11", { "sketchPlane" : qUnion([Q0])});
            skCircle(sketch, "E42", {"center": v(0, 0) * mm, "radius": 83.9 * mm, "construction": true});
            skLineSegment(sketch, "E43", {"start": v(-85.1, 21.63) * mm, "end": v(-77.54, 19.71) * mm, "construction": true});
            skPoint(sketch, "E44", {"position": v(-81.32, 20.67) * mm});
            skLineSegment(sketch, "E45", {"start": v(0, 0) * mm, "end": v(-87.8, -1.13) * mm, "construction": true});
            skCircle(sketch, "E46", {"center": v(-81.32, 20.67) * mm, "radius": 0.64 * mm});
            skCircle(sketch, "E47.1.0", {"center": v(-80.76, -22.76) * mm, "radius": 0.64 * mm});
            skCircle(sketch, "E47.2.0", {"center": v(-58.56, -60.09) * mm, "radius": 0.64 * mm});
            skCircle(sketch, "E47.3.0", {"center": v(-20.67, -81.32) * mm, "radius": 0.64 * mm});
            skCircle(sketch, "E47.4.0", {"center": v(22.76, -80.76) * mm, "radius": 0.64 * mm});
            skCircle(sketch, "E47.5.0", {"center": v(60.09, -58.56) * mm, "radius": 0.64 * mm});
            skCircle(sketch, "E47.6.0", {"center": v(81.32, -20.67) * mm, "radius": 0.64 * mm});
            skCircle(sketch, "E47.7.0", {"center": v(80.76, 22.76) * mm, "radius": 0.64 * mm});
            skCircle(sketch, "E47.8.0", {"center": v(58.56, 60.09) * mm, "radius": 0.64 * mm});
            skCircle(sketch, "E47.9.0", {"center": v(20.67, 81.32) * mm, "radius": 0.64 * mm});
            skCircle(sketch, "E47.10.0", {"center": v(-22.76, 80.76) * mm, "radius": 0.64 * mm});
            skCircle(sketch, "E47.11.0", {"center": v(-60.09, 58.56) * mm, "radius": 0.64 * mm});
            skCircle(sketch, "E48", {"center": v(0, 0) * mm, "radius": 68.5 * mm, "construction": true});
            skLineSegment(sketch, "E49", {"start": v(-64.6, -0.83) * mm, "end": v(-72.38, -0.93) * mm, "construction": true});
            skPoint(sketch, "E50", {"position": v(-68.5, -0.88) * mm});
            skCircle(sketch, "E51", {"center": v(-66.39, 16.88) * mm, "radius": 0.64 * mm});
            skCircle(sketch, "E52.1.0", {"center": v(-65.93, -18.58) * mm, "radius": 0.64 * mm});
            skCircle(sketch, "E52.2.0", {"center": v(-47.8, -49.05) * mm, "radius": 0.64 * mm});
            skCircle(sketch, "E52.3.0", {"center": v(-16.88, -66.39) * mm, "radius": 0.64 * mm});
            skCircle(sketch, "E52.4.0", {"center": v(18.58, -65.93) * mm, "radius": 0.64 * mm});
            skCircle(sketch, "E52.5.0", {"center": v(49.05, -47.8) * mm, "radius": 0.64 * mm});
            skCircle(sketch, "E52.6.0", {"center": v(66.39, -16.88) * mm, "radius": 0.64 * mm});
            skCircle(sketch, "E52.7.0", {"center": v(65.93, 18.58) * mm, "radius": 0.64 * mm});
            skCircle(sketch, "E52.8.0", {"center": v(47.8, 49.05) * mm, "radius": 0.64 * mm});
            skCircle(sketch, "E52.9.0", {"center": v(16.88, 66.39) * mm, "radius": 0.64 * mm});
            skCircle(sketch, "E52.10.0", {"center": v(-18.58, 65.93) * mm, "radius": 0.64 * mm});
            skCircle(sketch, "E52.11.0", {"center": v(-49.05, 47.8) * mm, "radius": 0.64 * mm});
            skSolve(sketch);
        }
        {
            var Q0;
            Q0 = qSketchRegion(id + "F11", true);
            extrude(context, id + "F12", {"entities" : qUnion([Q0]), "operationType" : NewBodyOperationType.REMOVE, "endBound" : BoundingType.THROUGH_ALL, "oppositeDirection" : true, "depth" : 22.86 * mm});
        }
        {
            var Q0;
            Q0=makeQuery(id+"F4.opExtrude","CAP_FACE",FACE,{"disambiguationData":[OSD([sQuery(id+"F3.wireOp",EDGE,"E22.0"),sQuery(id+"F3.wireOp",EDGE,"E23.0"),sQuery(id+"F3.wireOp",EDGE,"E24"),sQuery(id+"F3.wireOp",EDGE,"E25"),sQuery(id+"F3.wireOp",EDGE,"E26")])],"isStart":false});
            var sketch = newSketch(context, id + "F13", { "sketchPlane" : qUnion([Q0])});
            skCircle(sketch, "E53", {"center": v(0, 0) * mm, "radius": 80 * mm});
            skCircle(sketch, "E54", {"center": v(0, 0) * mm, "radius": 72.4 * mm});
            skLineSegment(sketch, "E55", {"start": v(-10.44, -79.33) * mm, "end": v(0, 0) * mm});
            skLineSegment(sketch, "E56", {"start": v(30.62, -73.92) * mm, "end": v(0, 0) * mm});
            skLineSegment(sketch, "E57", {"start": v(0, 0) * mm, "end": v(0, -80) * mm, "construction": true});
            skSolve(sketch);
        }
        {
            var Q0;
            {var subQ0=sQuery(id+"F13.wireOp",EDGE,"E55");var subQ1=sQuery(id+"F13.wireOp",EDGE,"E53");var subQ2=makeQuery(id+"F13.imprint","INTERSECT",VERTEX,{"derivedFrom":[subQ1,subQ0]});Q0=makeQuery(id+"F13.imprint","IMPRINT",FACE,{"disambiguationData":[TD([[makeQuery(id+"F13.imprint","IMPRINT",EDGE,{"disambiguationData":[TD([[subQ2,-1.0]])],"derivedFrom":subQ1}),1.0]])]});}
            extrude(context, id + "F14", {"entities" : qUnion([Q0]), "operationType" : NewBodyOperationType.REMOVE, "endBound" : BoundingType.UP_TO_NEXT, "oppositeDirection" : true, "depth" : 25.4 * mm});
        }
        {
            var Q0;
            Q0=makeQuery(id+"F6.opExtrude","SWEPT_FACE",FACE,{"disambiguationData":[OSD([sQuery(id+"F5.wireOp",EDGE,"E28.bottom")])]});
            var sketch = newSketch(context, id + "F15", { "sketchPlane" : qUnion([Q0])});
            skLineSegment(sketch, "E58", {"start": v(-57.15, -94.15) * mm, "end": v(57.15, -94.15) * mm, "construction": true});
            skCircle(sketch, "E59", {"center": v(-12.7, -94.15) * mm, "radius": 0.64 * mm});
            skCircle(sketch, "E60", {"center": v(12.7, -94.15) * mm, "radius": 0.64 * mm});
            skLineSegment(sketch, "E61", {"start": v(-12.7, -94.15) * mm, "end": v(12.7, -94.15) * mm, "construction": true});
            skPoint(sketch, "E62", {"position": v(0, -94.15) * mm});
            skSolve(sketch);
        }
        {
            var Q0;
            Q0 = qSketchRegion(id + "F15", true);
            extrude(context, id + "F16", {"entities" : qUnion([Q0]), "operationType" : NewBodyOperationType.REMOVE, "oppositeDirection" : true, "depth" : 25.4 * mm});
        }
    });
